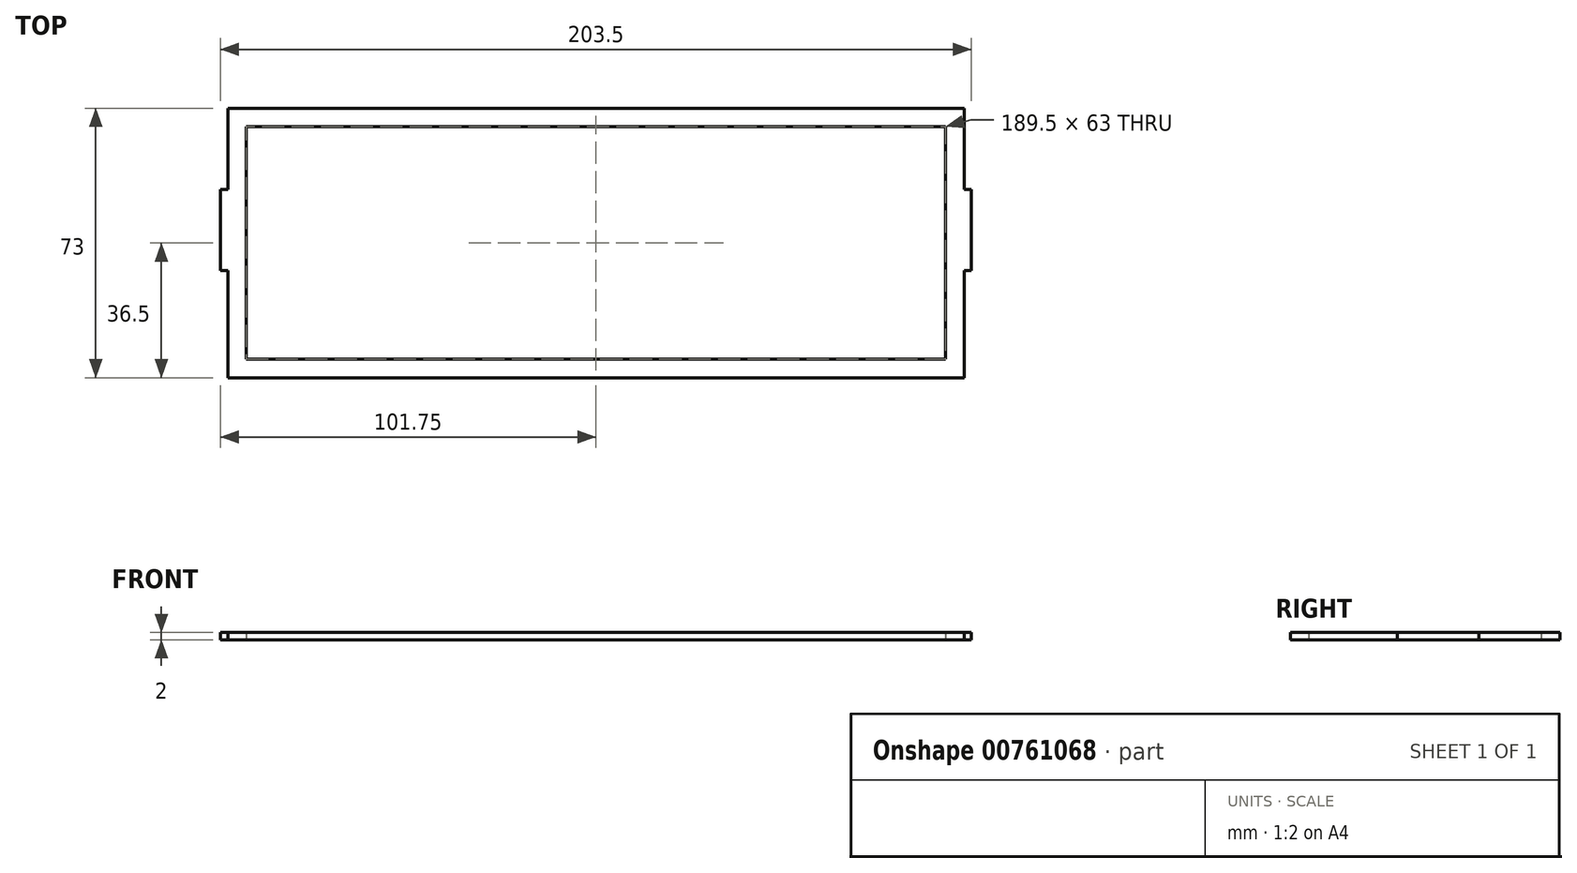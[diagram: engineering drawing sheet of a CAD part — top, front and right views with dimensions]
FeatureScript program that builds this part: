
annotation { "Feature Type Name" : "Feature", "Feature Type Description" : "" }
export const myFeature = defineFeature(function(context is Context, id is Id, definition is map)
    precondition{}
    {
        {
            var Q0;
            Q0=qCreatedBy(makeId("Top.planeOp"),FACE);
            var sketch = newSketch(context, id + "F0", { "sketchPlane" : qUnion([Q0])});
            skLineSegment(sketch, "E0", {"start": v(-103, 73) * mm, "end": v(-103, 51) * mm});
            skLineSegment(sketch, "E1", {"start": v(-103, 51) * mm, "end": v(-105, 51) * mm});
            skLineSegment(sketch, "E2", {"start": v(-103, 29) * mm, "end": v(-105, 29) * mm});
            skLineSegment(sketch, "E3", {"start": v(-105, 51) * mm, "end": v(-105, 29) * mm});
            skLineSegment(sketch, "E4", {"start": v(-103, 29) * mm, "end": v(-103, 0) * mm});
            skLineSegment(sketch, "E5", {"start": v(96.5, 73) * mm, "end": v(96.5, 51) * mm});
            skLineSegment(sketch, "E6", {"start": v(96.5, 51) * mm, "end": v(98.5, 51) * mm});
            skLineSegment(sketch, "E7", {"start": v(96.5, 29) * mm, "end": v(98.5, 29) * mm});
            skLineSegment(sketch, "E8", {"start": v(98.5, 51) * mm, "end": v(98.5, 29) * mm});
            skLineSegment(sketch, "E9", {"start": v(96.5, 29) * mm, "end": v(96.5, 0) * mm});
            skLineSegment(sketch, "E10", {"start": v(-103, 73) * mm, "end": v(96.5, 73) * mm});
            skLineSegment(sketch, "E11", {"start": v(96.5, 0) * mm, "end": v(-103, 0) * mm});
            skLineSegment(sketch, "E12", {"start": v(-98, 68) * mm, "end": v(91.5, 68) * mm});
            skLineSegment(sketch, "E13", {"start": v(91.5, 68) * mm, "end": v(91.5, 5) * mm});
            skLineSegment(sketch, "E14", {"start": v(91.5, 5) * mm, "end": v(-98, 5) * mm});
            skLineSegment(sketch, "E15", {"start": v(-98, 5) * mm, "end": v(-98, 68) * mm});
            skSolve(sketch);
        }
        {
            var Q0;
            Q0=qSketchRegion(id+"F0",true);
            extrude(context, id + "F1", {"entities" : qUnion([Q0]), "depth" : 2 * mm, "offsetDistance" : 25 * mm});
        }
    });
